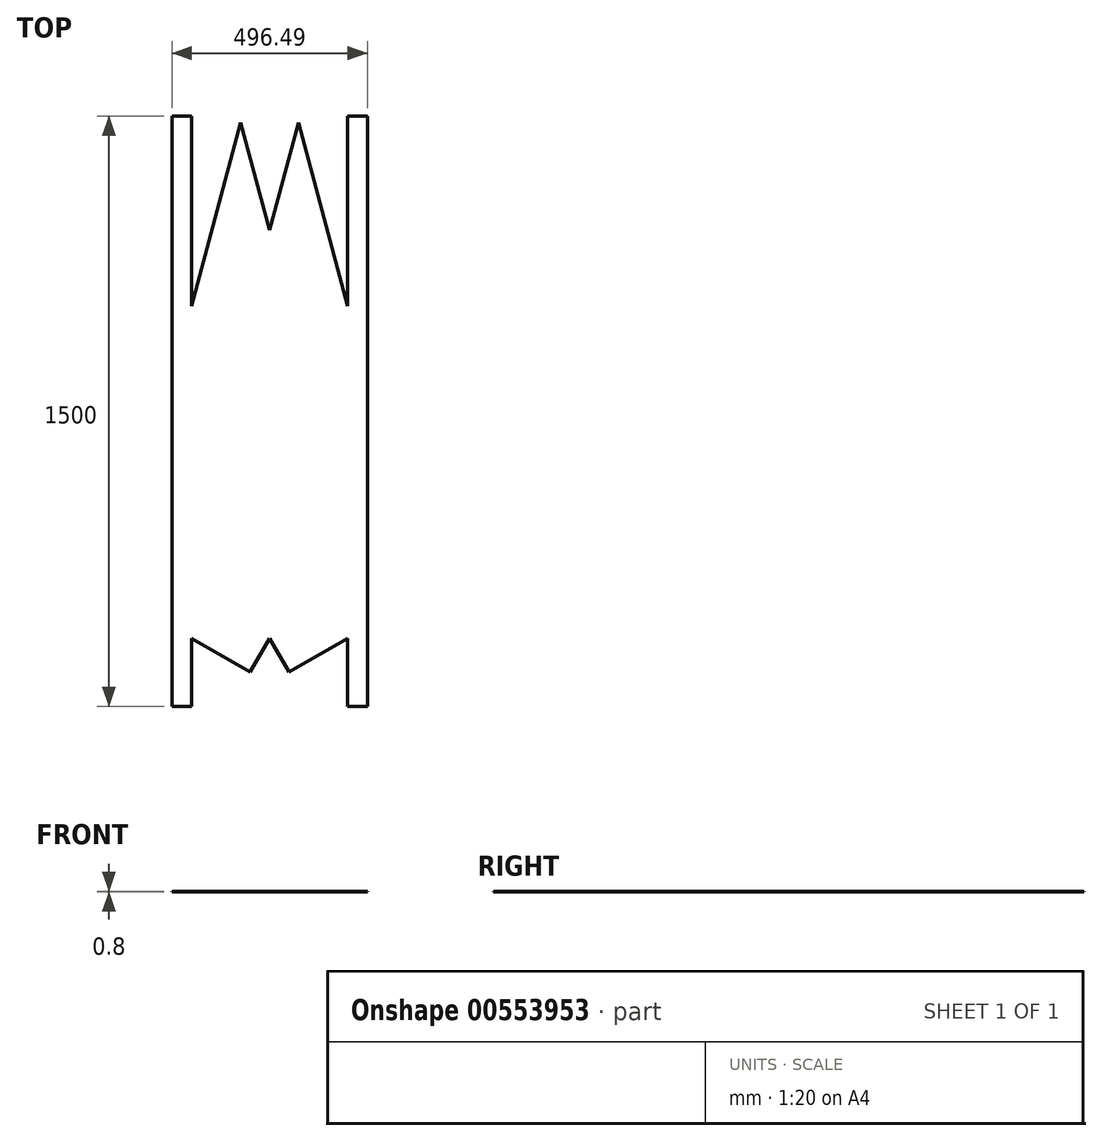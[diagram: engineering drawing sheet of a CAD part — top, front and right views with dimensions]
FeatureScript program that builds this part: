
annotation { "Feature Type Name" : "Feature", "Feature Type Description" : "" }
export const myFeature = defineFeature(function(context is Context, id is Id, definition is map)
    precondition{}
    {
        {
            var Q0;
            Q0=qCreatedBy(makeId("Top.planeOp"),FACE);
            var sketch = newSketch(context, id + "F0", { "sketchPlane" : qUnion([Q0])});
            skLineSegment(sketch, "E0.bottom", {"start": v(0, 0) * mm, "end": v(50, 0) * mm});
            skLineSegment(sketch, "E0.top", {"start": v(0, 173.2) * mm, "end": v(50, 173.2) * mm});
            skLineSegment(sketch, "E0.left", {"start": v(0, 0) * mm, "end": v(0, 173.2) * mm});
            skLineSegment(sketch, "E0.right", {"start": v(50, 0) * mm, "end": v(50, 173.2) * mm});
            skLineSegment(sketch, "E1.bottom", {"start": v(50, 173.2) * mm, "end": v(0, 173.2) * mm});
            skLineSegment(sketch, "E1.top", {"start": v(50, 1017.04) * mm, "end": v(0, 1017.04) * mm});
            skLineSegment(sketch, "E1.left", {"start": v(50, 173.2) * mm, "end": v(50, 1017.04) * mm});
            skLineSegment(sketch, "E1.right", {"start": v(0, 173.2) * mm, "end": v(0, 1017.04) * mm});
            skLineSegment(sketch, "E2.top", {"start": v(50, 1500) * mm, "end": v(0, 1500) * mm});
            skLineSegment(sketch, "E2.left", {"start": v(50, 1017.04) * mm, "end": v(50, 1500) * mm});
            skLineSegment(sketch, "E2.right", {"start": v(0, 1017.04) * mm, "end": v(0, 1500) * mm});
            skLineSegment(sketch, "E3", {"start": v(50, 1017.04) * mm, "end": v(175, 1483.54) * mm});
            skLineSegment(sketch, "E4", {"start": v(175, 1483.54) * mm, "end": v(248.25, 1210.19) * mm});
            skLineSegment(sketch, "E5", {"start": v(248.25, 1210.19) * mm, "end": v(50, 1017.04) * mm});
            skLineSegment(sketch, "E6", {"start": v(248.25, 1210.19) * mm, "end": v(248.25, 173.2) * mm});
            skLineSegment(sketch, "E7", {"start": v(248.25, 173.2) * mm, "end": v(50, 173.2) * mm});
            skLineSegment(sketch, "E8", {"start": v(248.25, 173.2) * mm, "end": v(198.68, 87.36) * mm});
            skLineSegment(sketch, "E9", {"start": v(198.68, 87.36) * mm, "end": v(50, 173.2) * mm});
            skLineSegment(sketch, "E10.MirrorCS", {"start": v(446.5, 1017.04) * mm, "end": v(496.5, 1017.04) * mm});
            skLineSegment(sketch, "E11.MirrorCS", {"start": v(446.5, 173.2) * mm, "end": v(496.5, 173.2) * mm});
            skLineSegment(sketch, "E12.MirrorCS", {"start": v(496.5, 173.2) * mm, "end": v(446.5, 173.2) * mm});
            skLineSegment(sketch, "E13.MirrorCS", {"start": v(496.5, 0) * mm, "end": v(446.5, 0) * mm});
            skLineSegment(sketch, "E14.MirrorCS", {"start": v(446.5, 1500) * mm, "end": v(496.5, 1500) * mm});
            skLineSegment(sketch, "E15.MirrorCS", {"start": v(248.25, 173.2) * mm, "end": v(297.8, 87.36) * mm});
            skLineSegment(sketch, "E16.MirrorCS", {"start": v(446.5, 1017.04) * mm, "end": v(446.5, 1500) * mm});
            skLineSegment(sketch, "E17.MirrorCS", {"start": v(321.5, 1483.54) * mm, "end": v(248.25, 1210.19) * mm});
            skLineSegment(sketch, "E18.MirrorCS", {"start": v(248.25, 1210.19) * mm, "end": v(446.5, 1017.04) * mm});
            skLineSegment(sketch, "E19.MirrorCS", {"start": v(496.5, 173.2) * mm, "end": v(496.5, 1017.04) * mm});
            skLineSegment(sketch, "E20.MirrorCS", {"start": v(496.5, 1017.04) * mm, "end": v(496.5, 1500) * mm});
            skLineSegment(sketch, "E21.MirrorCS", {"start": v(446.5, 173.2) * mm, "end": v(446.5, 1017.04) * mm});
            skLineSegment(sketch, "E22.MirrorCS", {"start": v(496.5, 0) * mm, "end": v(496.5, 173.2) * mm});
            skLineSegment(sketch, "E23.MirrorCS", {"start": v(446.5, 1017.04) * mm, "end": v(321.5, 1483.54) * mm});
            skLineSegment(sketch, "E24.MirrorCS", {"start": v(446.5, 0) * mm, "end": v(446.5, 173.2) * mm});
            skLineSegment(sketch, "E25.MirrorCS", {"start": v(297.8, 87.36) * mm, "end": v(446.5, 173.2) * mm});
            skLineSegment(sketch, "E26.MirrorCS", {"start": v(248.25, 173.2) * mm, "end": v(446.5, 173.2) * mm});
            skSolve(sketch);
        }
        {
            var Q0;
            Q0=qSketchRegion(id+"F0",true);
            extrude(context, id + "F1", {"entities" : qUnion([Q0]), "endBound" : BoundingType.SYMMETRIC, "depth" : 0.8 * mm});
        }
    });
